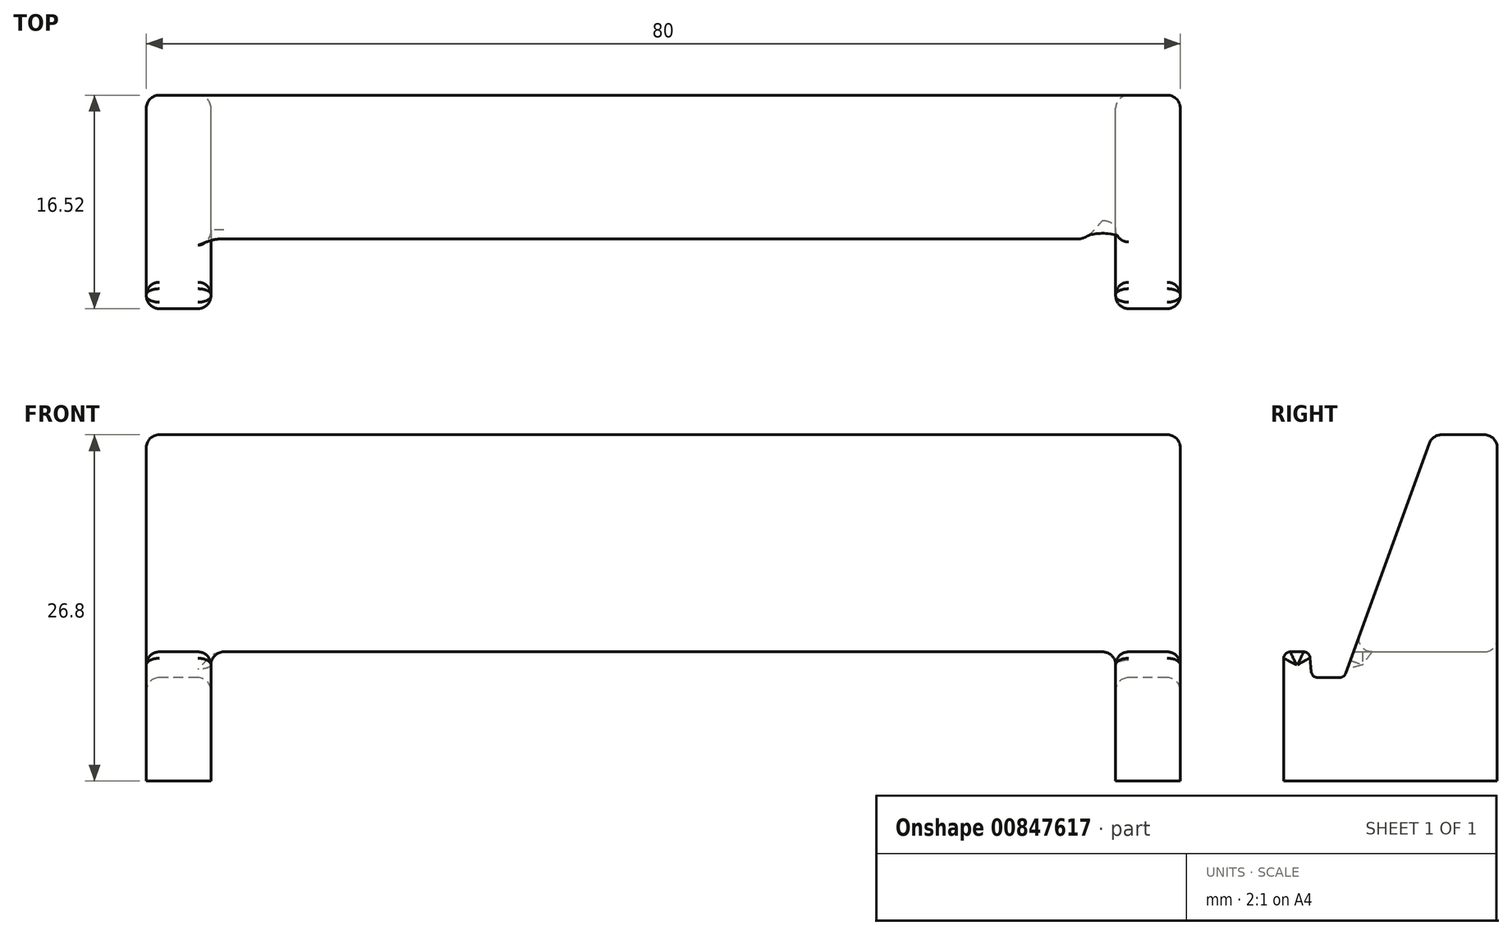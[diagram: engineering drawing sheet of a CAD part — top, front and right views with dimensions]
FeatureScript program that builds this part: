
annotation { "Feature Type Name" : "Feature", "Feature Type Description" : "" }
export const myFeature = defineFeature(function(context is Context, id is Id, definition is map)
    precondition{}
    {
        {
            var Q0;
            Q0=qCreatedBy(makeId("Right.planeOp"),FACE);
            var sketch = newSketch(context, id + "F0", { "sketchPlane" : qUnion([Q0])});
            skLineSegment(sketch, "E0", {"start": v(-15.51, -14.4) * mm, "end": v(-13.82, -14.4) * mm});
            skLineSegment(sketch, "E1", {"start": v(-13.35, -14.06) * mm, "end": v(-6.77, 4) * mm});
            skLineSegment(sketch, "E2", {"start": v(-16.01, -13.94) * mm, "end": v(-16.1, -12.86) * mm});
            skLineSegment(sketch, "E3", {"start": v(-16.6, -12.4) * mm, "end": v(-17.65, -12.4) * mm});
            skLineSegment(sketch, "E4", {"start": v(-18.15, -12.9) * mm, "end": v(-18.15, -22.4) * mm});
            skLineSegment(sketch, "E5", {"start": v(-6.21, 4.4) * mm, "end": v(-1.63, 4.4) * mm});
            skLineSegment(sketch, "E6", {"start": v(-1.63, 4.4) * mm, "end": v(-1.63, -22.4) * mm});
            skLineSegment(sketch, "E7", {"start": v(-1.63, -22.4) * mm, "end": v(-18.15, -22.4) * mm});
            skPoint(sketch, "E8.visualSharp", {"position": v(-6.63, 4.4) * mm});
            skPoint(sketch, "E9.visualSharp", {"position": v(-15.97, -14.4) * mm});
            skArc(sketch, "E9.filletArc", {"start": v(-16.01, -13.94) * mm, "mid": v(-15.85, -14.26) * mm, "end": v(-15.51, -14.4) * mm});
            skPoint(sketch, "E10.visualSharp", {"position": v(-13.47, -14.4) * mm});
            skArc(sketch, "E10.filletArc", {"start": v(-13.82, -14.4) * mm, "mid": v(-13.53, -14.3) * mm, "end": v(-13.35, -14.06) * mm});
            skPoint(sketch, "E11.visualSharp", {"position": v(-16.15, -12.4) * mm});
            skArc(sketch, "E11.filletArc", {"start": v(-16.1, -12.86) * mm, "mid": v(-16.27, -12.53) * mm, "end": v(-16.6, -12.4) * mm});
            skPoint(sketch, "E12.visualSharp", {"position": v(-18.15, -12.4) * mm});
            skArc(sketch, "E12.filletArc", {"start": v(-17.65, -12.4) * mm, "mid": v(-18, -12.55) * mm, "end": v(-18.15, -12.9) * mm});
            skLineSegment(sketch, "E13", {"start": v(-6.21, 4.4) * mm, "end": v(-6.63, 4.4) * mm});
            skLineSegment(sketch, "E14", {"start": v(-6.77, 4) * mm, "end": v(-6.63, 4.4) * mm});
            skSolve(sketch);
        }
        {
            var Q0;
            Q0=makeQuery(id+"F0.imprint","IMPRINT",FACE,{"disambiguationData":[TD([[makeQuery(id+"F0.imprint","IMPRINT",EDGE,{"derivedFrom":sQuery(id+"F0.wireOp",EDGE,"E0")}),-1.0]])]});
            extrude(context, id + "F1", {"entities" : qUnion([Q0]), "depth" : 80 * mm, "offsetDistance" : 25 * mm});
        }
        {
            var Q0;
            Q0=qCreatedBy(makeId("Front.planeOp"),FACE);
            var sketch = newSketch(context, id + "F2", { "sketchPlane" : qUnion([Q0])});
            skLineSegment(sketch, "E15.bottom", {"start": v(6, -12.4) * mm, "end": v(74, -12.4) * mm});
            skLineSegment(sketch, "E15.top", {"start": v(5, -22.4) * mm, "end": v(75, -22.4) * mm});
            skLineSegment(sketch, "E15.left", {"start": v(5, -13.4) * mm, "end": v(5, -22.4) * mm});
            skLineSegment(sketch, "E15.right", {"start": v(75, -13.4) * mm, "end": v(75, -22.4) * mm});
            skPoint(sketch, "E16.visualSharp", {"position": v(75, -12.4) * mm});
            skPoint(sketch, "E17.visualSharp", {"position": v(5, -12.4) * mm});
            skLineSegment(sketch, "E18", {"start": v(6, -12.4) * mm, "end": v(5, -12.4) * mm});
            skLineSegment(sketch, "E19", {"start": v(5, -13.4) * mm, "end": v(5, -12.4) * mm});
            skLineSegment(sketch, "E20", {"start": v(75, -13.4) * mm, "end": v(75, -12.4) * mm});
            skLineSegment(sketch, "E21", {"start": v(74, -12.4) * mm, "end": v(75, -12.4) * mm});
            skSolve(sketch);
        }
        {
            var Q0;
            Q0 = qSketchRegion(id + "F2", true);
            extrude(context, id + "F3", {"entities" : qUnion([Q0]), "operationType" : NewBodyOperationType.REMOVE, "depth" : 25 * mm, "offsetDistance" : 25 * mm});
        }
        {
            var Q0;
            Q0=makeQuery(id+"F1.opExtrude","SWEPT_EDGE",EDGE,{"disambiguationData":[OSD([sQuery(id+"F0.wireOp",EDGE,"E5"),sQuery(id+"F0.wireOp",EDGE,"E6")])]});
            var Q1;
            Q1=makeQuery(id+"F3.boolean.opBoolean","INTERSECT",EDGE,{"derivedFrom":[makeQuery(id+"F1.opExtrude","SWEPT_FACE",FACE,{"disambiguationData":[OSD([sQuery(id+"F0.wireOp",EDGE,"E6")])]}),makeQuery(id+"F3.opExtrude","SWEPT_FACE",FACE,{"disambiguationData":[OSD([sQuery(id+"F2.wireOp",EDGE,"E15.bottom")])]})]});
            var Q2;
            Q2=makeQuery(id+"F1.opExtrude","SWEPT_EDGE",EDGE,{"disambiguationData":[OSD([sQuery(id+"F0.wireOp",EDGE,"E13"),sQuery(id+"F0.wireOp",EDGE,"E14")])]});
            var Q3;
            Q3=makeQuery(id+"F3.boolean.opBoolean","INTERSECT",EDGE,{"derivedFrom":[makeQuery(id+"F1.opExtrude","SWEPT_FACE",FACE,{"disambiguationData":[OSD([sQuery(id+"F0.wireOp",EDGE,"E4")])]}),makeQuery(id+"F3.opExtrude","SWEPT_FACE",FACE,{"disambiguationData":[OSD([sQuery(id+"F2.wireOp",EDGE,"E15.left")])]})]});
            fillet(context, id + "F4", {"entities" : qUnion([Q0, Q1, Q2, Q3]), "radius" : 1 * mm, "tangentPropagation" : true, "allowEdgeOverflow" : false});
        }
        {
            var Q0;
            {var subQ0=sQuery(id+"F2.wireOp",EDGE,"E21");var subQ1=sQuery(id+"F2.wireOp",EDGE,"E20");Q0=makeQuery(id+"F3.boolean.opBoolean","COPY",EDGE,{"disambiguationData":[topologyDisambiguationEdgeConnected([makeQuery(id+"F3.opExtrude","SWEPT_FACE",FACE,{"disambiguationData":[OSD([sQuery(id+"F2.wireOp",EDGE,"E15.bottom"),sQuery(id+"F2.wireOp",EDGE,"E18"),subQ0])]})])],"derivedFrom":makeQuery(id+"F3.opExtrude","SWEPT_EDGE",EDGE,{"disambiguationData":[OSD([subQ1,subQ0])]})});}
            var Q1;
            {var subQ0=sQuery(id+"F2.wireOp",EDGE,"E18");var subQ1=sQuery(id+"F2.wireOp",EDGE,"E19");Q1=makeQuery(id+"F3.boolean.opBoolean","COPY",EDGE,{"disambiguationData":[topologyDisambiguationEdgeConnected([makeQuery(id+"F3.opExtrude","SWEPT_FACE",FACE,{"disambiguationData":[OSD([sQuery(id+"F2.wireOp",EDGE,"E15.bottom"),subQ0,sQuery(id+"F2.wireOp",EDGE,"E21")])]})])],"derivedFrom":makeQuery(id+"F3.opExtrude","SWEPT_EDGE",EDGE,{"disambiguationData":[OSD([subQ0,subQ1])]})});}
            var Q2;
            Q2=makeQuery(id+"F3.boolean.opBoolean","INTERSECT",EDGE,{"derivedFrom":[makeQuery(id+"F1.opExtrude","SWEPT_FACE",FACE,{"disambiguationData":[OSD([sQuery(id+"F0.wireOp",EDGE,"E6")])]}),makeQuery(id+"F3.opExtrude","SWEPT_FACE",FACE,{"disambiguationData":[OSD([sQuery(id+"F2.wireOp",EDGE,"E15.left"),sQuery(id+"F2.wireOp",EDGE,"E19")])]})]});
            var Q3;
            Q3=makeQuery(id+"F3.boolean.opBoolean","INTERSECT",EDGE,{"derivedFrom":[makeQuery(id+"F1.opExtrude","SWEPT_FACE",FACE,{"disambiguationData":[OSD([sQuery(id+"F0.wireOp",EDGE,"E6")])]}),makeQuery(id+"F3.opExtrude","SWEPT_FACE",FACE,{"disambiguationData":[OSD([sQuery(id+"F2.wireOp",EDGE,"E15.right"),sQuery(id+"F2.wireOp",EDGE,"E20")])]})]});
            var Q4;
            Q4=makeQuery(id+"F3.boolean.opBoolean","INTERSECT",EDGE,{"derivedFrom":[makeQuery(id+"F1.opExtrude","SWEPT_FACE",FACE,{"disambiguationData":[OSD([sQuery(id+"F0.wireOp",EDGE,"E4")])]}),makeQuery(id+"F3.opExtrude","SWEPT_FACE",FACE,{"disambiguationData":[OSD([sQuery(id+"F2.wireOp",EDGE,"E15.right"),sQuery(id+"F2.wireOp",EDGE,"E20")])]})]});
            fillet(context, id + "F5", {"entities" : qUnion([Q0, Q1, Q2, Q3, Q4]), "radius" : 1 * mm, "tangentPropagation" : true, "allowEdgeOverflow" : false});
        }
        {
            var Q0;
            Q0=makeQuery(id+"F1.opExtrude","CAP_EDGE",EDGE,{"disambiguationData":[OSD([sQuery(id+"F0.wireOp",EDGE,"E1"),sQuery(id+"F0.wireOp",EDGE,"E14")])],"isStart":true});
            var Q1;
            Q1=makeQuery(id+"F1.opExtrude","CAP_EDGE",EDGE,{"disambiguationData":[OSD([sQuery(id+"F0.wireOp",EDGE,"E6")])],"isStart":true});
            var Q2;
            Q2=makeQuery(id+"F1.opExtrude","CAP_EDGE",EDGE,{"disambiguationData":[OSD([sQuery(id+"F0.wireOp",EDGE,"E1"),sQuery(id+"F0.wireOp",EDGE,"E14")])],"isStart":false});
            fillet(context, id + "F6", {"entities" : qUnion([Q0, Q1, Q2]), "radius" : 1 * mm, "tangentPropagation" : true, "allowEdgeOverflow" : false});
        }
    });
